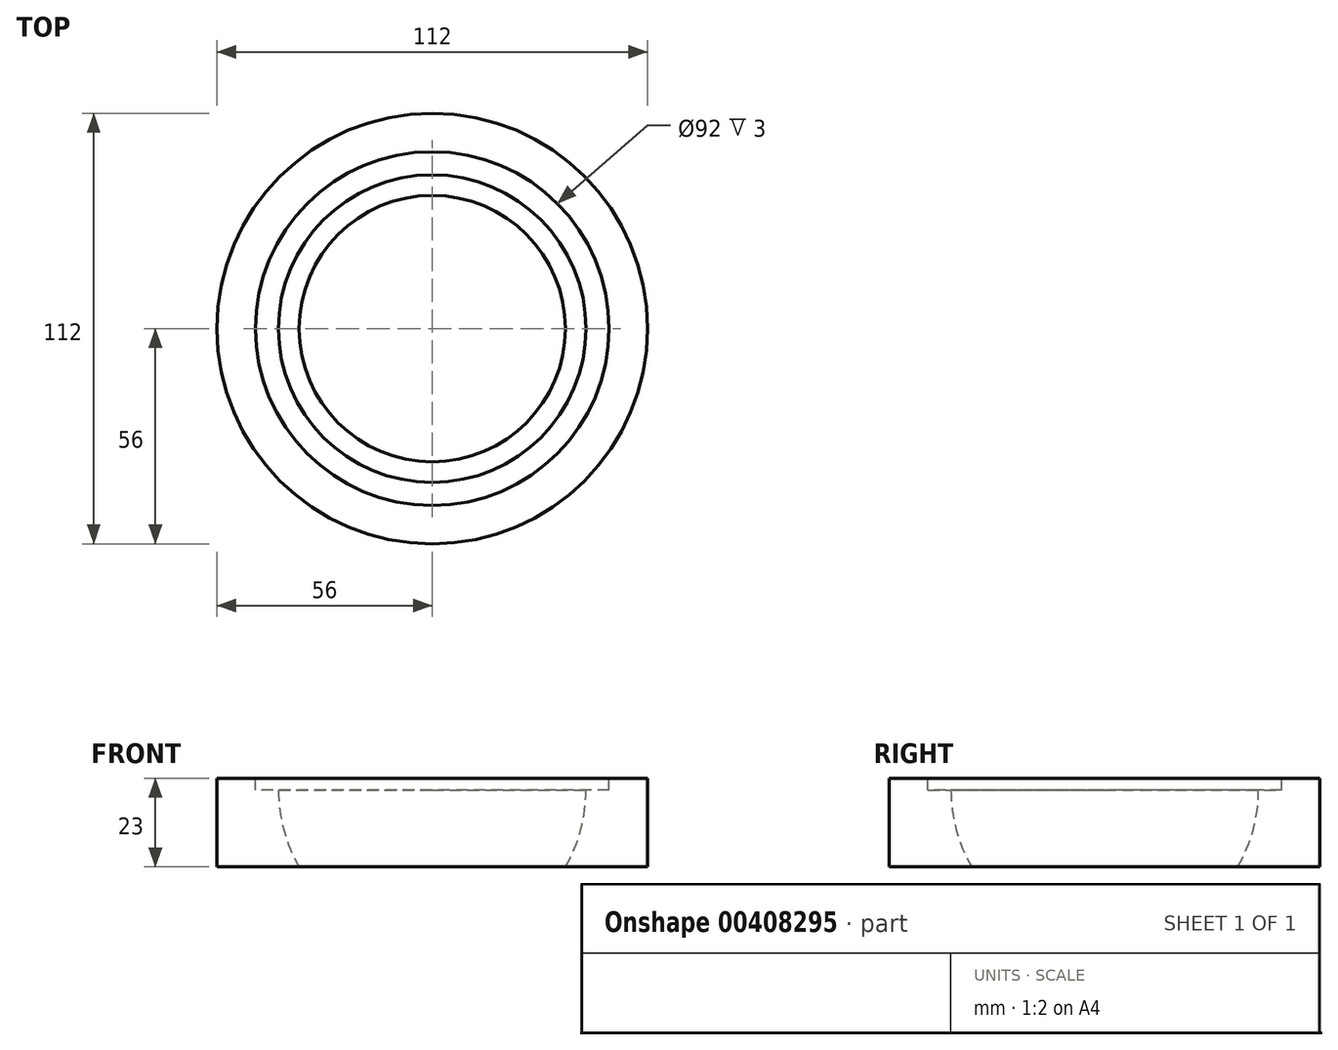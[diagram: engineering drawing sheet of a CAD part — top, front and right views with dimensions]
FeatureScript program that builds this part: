
annotation { "Feature Type Name" : "Feature", "Feature Type Description" : "" }
export const myFeature = defineFeature(function(context is Context, id is Id, definition is map)
    precondition{}
    {
        {
            var Q0;
            Q0=qCreatedBy(makeId("Top.planeOp"),FACE);
            var sketch = newSketch(context, id + "F0", { "sketchPlane" : qUnion([Q0])});
            skCircle(sketch, "E0", {"center": v(0, 0) * mm, "radius": 56 * mm});
            skSolve(sketch);
        }
        {
            var Q0;
            Q0=makeQuery(id+"F0.imprint","IMPRINT",FACE,{"disambiguationData":[TD([[makeQuery(id+"F0.imprint","IMPRINT",EDGE,{"derivedFrom":sQuery(id+"F0.wireOp",EDGE,"E0")}),1.0]])]});
            extrude(context, id + "F1", {"entities" : qUnion([Q0]), "oppositeDirection" : true, "depth" : 23 * mm});
        }
        {
            var Q0;
            Q0=makeQuery(id+"F1.opExtrude","CAP_FACE",FACE,{"disambiguationData":[OSD([sQuery(id+"F0.wireOp",EDGE,"E0")])],"isStart":true});
            var sketch = newSketch(context, id + "F2", { "sketchPlane" : qUnion([Q0])});
            skCircle(sketch, "E1", {"center": v(0, 0) * mm, "radius": 46 * mm});
            skSolve(sketch);
        }
        {
            var Q0;
            Q0=makeQuery(id+"F2.imprint","IMPRINT",FACE,{"disambiguationData":[TD([[makeQuery(id+"F2.imprint","IMPRINT",EDGE,{"derivedFrom":sQuery(id+"F2.wireOp",EDGE,"E1")}),1.0]])]});
            extrude(context, id + "F3", {"entities" : qUnion([Q0]), "operationType" : NewBodyOperationType.REMOVE, "oppositeDirection" : true, "depth" : 3 * mm});
        }
        {
            var Q0;
            Q0=makeQuery(id+"F3.boolean.opBoolean","COPY",FACE,{"derivedFrom":makeQuery(id+"F3.opExtrude","CAP_FACE",FACE,{"disambiguationData":[OSD([sQuery(id+"F2.wireOp",EDGE,"E1")])],"isStart":false})});
            var sketch = newSketch(context, id + "F4", { "sketchPlane" : qUnion([Q0])});
            skArc(sketch, "E2", {"start": v(0, 40) * mm, "mid": v(-40, 0) * mm, "end": v(0, -40) * mm});
            skLineSegment(sketch, "E3", {"start": v(0, -40) * mm, "end": v(0, 40) * mm});
            skSolve(sketch);
        }
        {
            var Q0;
            Q0=makeQuery(id+"F4.imprint","IMPRINT",FACE,{"disambiguationData":[TD([[makeQuery(id+"F4.imprint","IMPRINT",EDGE,{"derivedFrom":sQuery(id+"F4.wireOp",EDGE,"E2")}),1.0]])]});
            var Q1;
            Q1=sQuery(id+"F4.wireOp",EDGE,"E3");
            revolve(context, id + "F5", {"operationType" : NewBodyOperationType.REMOVE, "entities" : qUnion([Q0]), "axis" : qUnion([Q1]), "revolveType" : RevolveType.ONE_DIRECTION, "oppositeDirection" : true, "angle" : 180 * degree});
        }
    });
